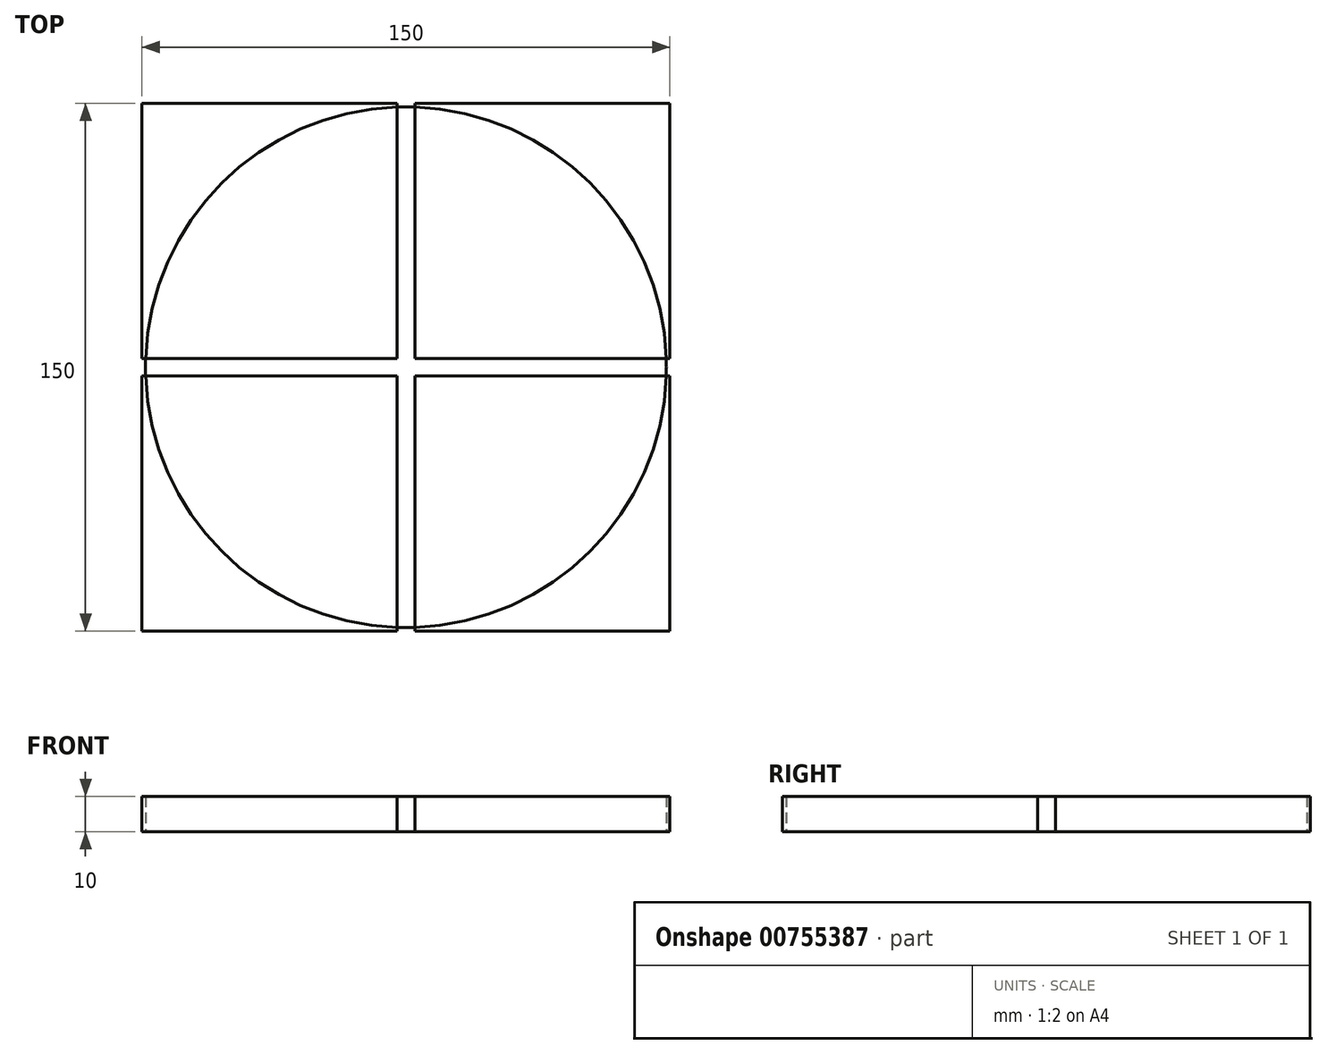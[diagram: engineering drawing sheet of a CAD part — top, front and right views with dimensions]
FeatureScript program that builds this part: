
annotation { "Feature Type Name" : "Feature", "Feature Type Description" : "" }
export const myFeature = defineFeature(function(context is Context, id is Id, definition is map)
    precondition{}
    {
        {
            var Q0;
            Q0=qCreatedBy(makeId("Top.planeOp"),FACE);
            var sketch = newSketch(context, id + "F0", { "sketchPlane" : qUnion([Q0])});
            skLineSegment(sketch, "E0.bottom", {"start": v(75, -75) * mm, "end": v(-75, -75) * mm});
            skLineSegment(sketch, "E0.top", {"start": v(75, 75) * mm, "end": v(-75, 75) * mm});
            skLineSegment(sketch, "E0.left", {"start": v(75, -75) * mm, "end": v(75, 75) * mm});
            skLineSegment(sketch, "E0.right", {"start": v(-75, -75) * mm, "end": v(-75, 75) * mm});
            skPoint(sketch, "E0.middle", {"position": v(0, 0) * mm});
            skLineSegment(sketch, "E1.bottom", {"start": v(2.5, -75) * mm, "end": v(-2.5, -75) * mm});
            skLineSegment(sketch, "E1.top", {"start": v(2.5, 75) * mm, "end": v(-2.5, 75) * mm});
            skLineSegment(sketch, "E1.left", {"start": v(2.5, -75) * mm, "end": v(2.5, 75) * mm});
            skLineSegment(sketch, "E1.right", {"start": v(-2.5, -75) * mm, "end": v(-2.5, 75) * mm});
            skLineSegment(sketch, "E2.bottom", {"start": v(75, -2.5) * mm, "end": v(-75, -2.5) * mm});
            skLineSegment(sketch, "E2.top", {"start": v(75, 2.5) * mm, "end": v(-75, 2.5) * mm});
            skLineSegment(sketch, "E2.left", {"start": v(75, -2.5) * mm, "end": v(75, 2.5) * mm});
            skLineSegment(sketch, "E2.right", {"start": v(-75, -2.5) * mm, "end": v(-75, 2.5) * mm});
            skCircle(sketch, "E3", {"center": v(0, 0) * mm, "radius": 74 * mm});
            skSolve(sketch);
        }
        {
            var Q0;
            {var subQ0=sQuery(id+"F0.wireOp",EDGE,"E2.bottom");var subQ1=sQuery(id+"F0.wireOp",EDGE,"E1.left");var subQ2=makeQuery(id+"F0.imprint","INTERSECT",VERTEX,{"derivedFrom":[subQ1,subQ0]});Q0=makeQuery(id+"F0.imprint","IMPRINT",FACE,{"disambiguationData":[TD([[makeQuery(id+"F0.imprint","IMPRINT",EDGE,{"disambiguationData":[TD([[subQ2,-1.0]])],"derivedFrom":subQ1}),-1.0]])]});}
            var Q1;
            {var subQ0=sQuery(id+"F0.wireOp",EDGE,"E2.top");var subQ1=sQuery(id+"F0.wireOp",EDGE,"E1.left");var subQ2=makeQuery(id+"F0.imprint","INTERSECT",VERTEX,{"derivedFrom":[subQ1,subQ0]});Q1=makeQuery(id+"F0.imprint","IMPRINT",FACE,{"disambiguationData":[TD([[makeQuery(id+"F0.imprint","IMPRINT",EDGE,{"disambiguationData":[TD([[subQ2,-1.0]])],"derivedFrom":subQ1}),1.0]])]});}
            var Q2;
            {var subQ0=sQuery(id+"F0.wireOp",EDGE,"E3");var subQ1=sQuery(id+"F0.wireOp",EDGE,"E1.left");var subQ2=makeQuery(id+"F0.imprint","INTERSECT",VERTEX,{"disambiguationData":[OD(0.0)],"derivedFrom":[subQ1,subQ0]});Q2=makeQuery(id+"F0.imprint","IMPRINT",FACE,{"disambiguationData":[TD([[makeQuery(id+"F0.imprint","IMPRINT",EDGE,{"disambiguationData":[TD([[subQ2,-1.0]])],"derivedFrom":subQ1}),1.0]])]});}
            var Q3;
            {var subQ0=sQuery(id+"F0.wireOp",EDGE,"E2.right");Q3=makeQuery(id+"F0.imprint","IMPRINT",FACE,{"disambiguationData":[TD([[makeQuery(id+"F0.imprint","IMPRINT",EDGE,{"derivedFrom":subQ0}),-1.0]])]});}
            var Q4;
            {var subQ0=sQuery(id+"F0.wireOp",EDGE,"E1.top");Q4=makeQuery(id+"F0.imprint","IMPRINT",FACE,{"disambiguationData":[TD([[makeQuery(id+"F0.imprint","IMPRINT",EDGE,{"derivedFrom":subQ0}),1.0]])]});}
            var Q5;
            {var subQ0=sQuery(id+"F0.wireOp",EDGE,"E1.bottom");Q5=makeQuery(id+"F0.imprint","IMPRINT",FACE,{"disambiguationData":[TD([[makeQuery(id+"F0.imprint","IMPRINT",EDGE,{"derivedFrom":subQ0}),-1.0]])]});}
            var Q6;
            {var subQ0=sQuery(id+"F0.wireOp",EDGE,"E2.bottom");var subQ1=sQuery(id+"F0.wireOp",EDGE,"E1.right");var subQ2=makeQuery(id+"F0.imprint","INTERSECT",VERTEX,{"derivedFrom":[subQ1,subQ0]});Q6=makeQuery(id+"F0.imprint","IMPRINT",FACE,{"disambiguationData":[TD([[makeQuery(id+"F0.imprint","IMPRINT",EDGE,{"disambiguationData":[TD([[subQ2,-1.0]])],"derivedFrom":subQ1}),1.0]])]});}
            var Q7;
            {var subQ0=sQuery(id+"F0.wireOp",EDGE,"E2.left");Q7=makeQuery(id+"F0.imprint","IMPRINT",FACE,{"disambiguationData":[TD([[makeQuery(id+"F0.imprint","IMPRINT",EDGE,{"derivedFrom":subQ0}),1.0]])]});}
            var Q8;
            {var subQ0=sQuery(id+"F0.wireOp",EDGE,"E2.bottom");var subQ1=sQuery(id+"F0.wireOp",EDGE,"E1.left");var subQ2=makeQuery(id+"F0.imprint","INTERSECT",VERTEX,{"derivedFrom":[subQ1,subQ0]});Q8=makeQuery(id+"F0.imprint","IMPRINT",FACE,{"disambiguationData":[TD([[makeQuery(id+"F0.imprint","IMPRINT",EDGE,{"disambiguationData":[TD([[subQ2,-1.0]])],"derivedFrom":subQ1}),1.0]])]});}
            var Q9;
            {var subQ3=sQuery(id+"F0.wireOp",EDGE,"E3");var subQ5=sQuery(id+"F0.wireOp",EDGE,"E1.right");var subQ8=makeQuery(id+"F0.imprint","INTERSECT",VERTEX,{"disambiguationData":[OD(0.0)],"derivedFrom":[subQ5,subQ3]});Q9=makeQuery(id+"F0.imprint","IMPRINT",FACE,{"disambiguationData":[TD([[makeQuery(id+"F0.imprint","IMPRINT",EDGE,{"disambiguationData":[TD([[subQ8,1.0]])],"derivedFrom":subQ3}),-1.0]])]});}
            var Q10;
            {var subQ5=sQuery(id+"F0.wireOp",EDGE,"E3");var subQ7=sQuery(id+"F0.wireOp",EDGE,"E1.left");var subQ9=makeQuery(id+"F0.imprint","INTERSECT",VERTEX,{"disambiguationData":[OD(0.0)],"derivedFrom":[subQ7,subQ5]});Q10=makeQuery(id+"F0.imprint","IMPRINT",FACE,{"disambiguationData":[TD([[makeQuery(id+"F0.imprint","IMPRINT",EDGE,{"disambiguationData":[TD([[subQ9,-1.0]])],"derivedFrom":subQ5}),-1.0]])]});}
            var Q11;
            {var subQ3=sQuery(id+"F0.wireOp",EDGE,"E3");var subQ7=sQuery(id+"F0.wireOp",EDGE,"E1.right");var subQ9=makeQuery(id+"F0.imprint","INTERSECT",VERTEX,{"disambiguationData":[OD(1.0)],"derivedFrom":[subQ7,subQ3]});Q11=makeQuery(id+"F0.imprint","IMPRINT",FACE,{"disambiguationData":[TD([[makeQuery(id+"F0.imprint","IMPRINT",EDGE,{"disambiguationData":[TD([[subQ9,-1.0]])],"derivedFrom":subQ3}),-1.0]])]});}
            var Q12;
            {var subQ0=sQuery(id+"F0.wireOp",EDGE,"E1.left");var subQ3=sQuery(id+"F0.wireOp",EDGE,"E3");var subQ4=makeQuery(id+"F0.imprint","INTERSECT",VERTEX,{"disambiguationData":[OD(1.0)],"derivedFrom":[subQ0,subQ3]});Q12=makeQuery(id+"F0.imprint","IMPRINT",FACE,{"disambiguationData":[TD([[makeQuery(id+"F0.imprint","IMPRINT",EDGE,{"disambiguationData":[TD([[subQ4,1.0]])],"derivedFrom":subQ3}),-1.0]])]});}
            extrude(context, id + "F1", {"entities" : qUnion([Q0, Q1, Q2, Q3, Q4, Q5, Q6, Q7, Q8, Q9, Q10, Q11, Q12]), "depth" : 10 * mm, "offsetDistance" : 25 * mm});
        }
    });
